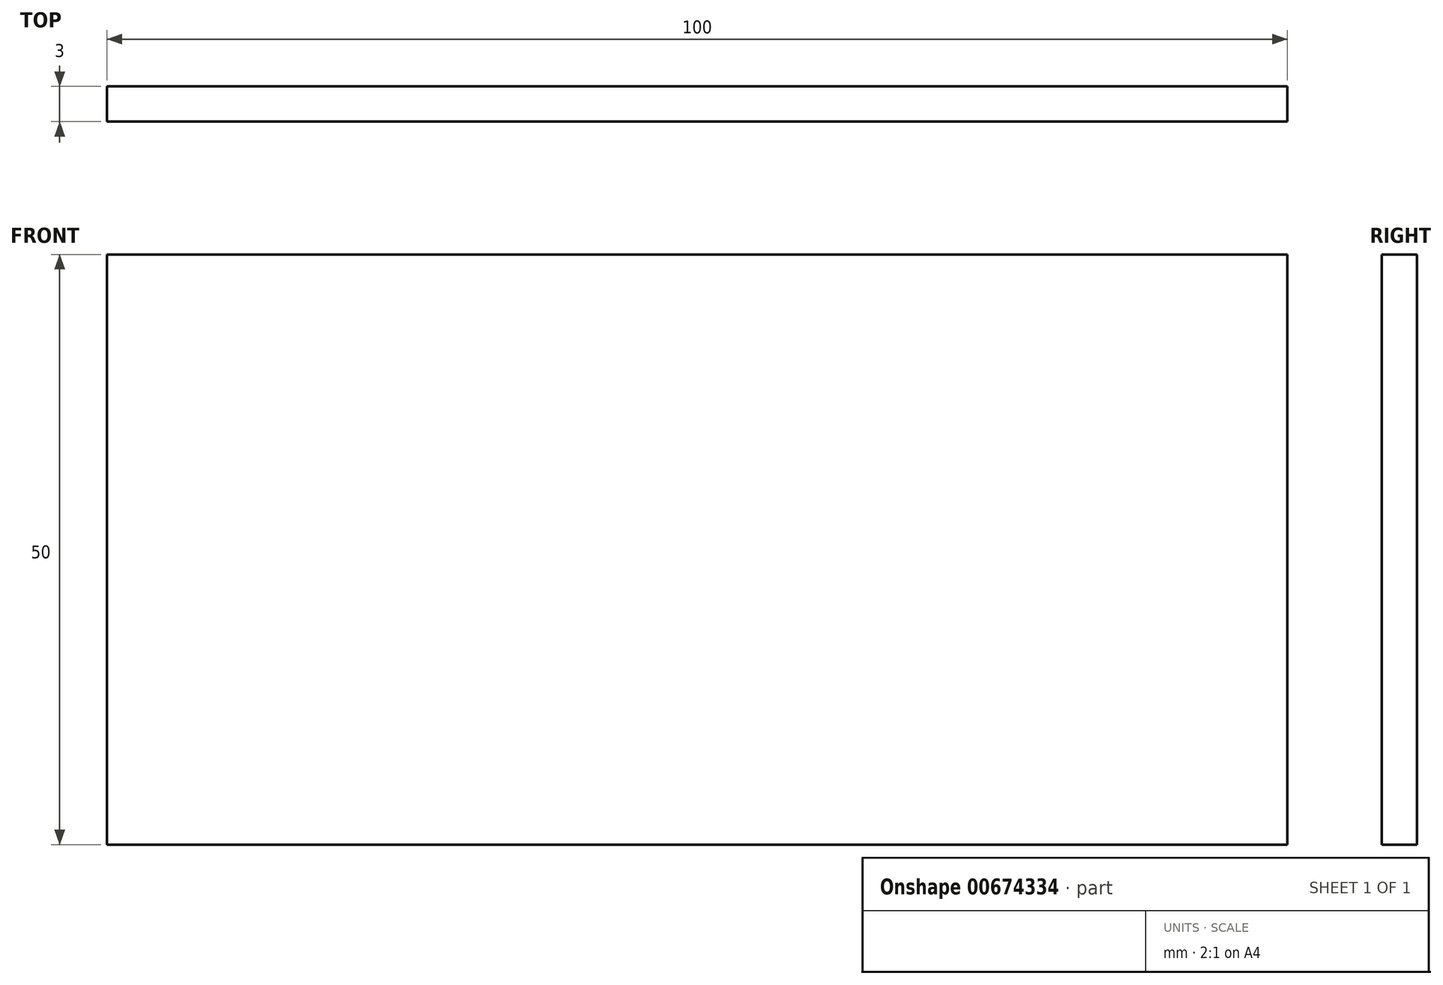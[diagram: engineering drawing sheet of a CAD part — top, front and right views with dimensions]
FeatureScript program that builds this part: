
annotation { "Feature Type Name" : "Feature", "Feature Type Description" : "" }
export const myFeature = defineFeature(function(context is Context, id is Id, definition is map)
    precondition{}
    {
        {
            var Q0;
            Q0=qCreatedBy(makeId("Front.planeOp"),FACE);
            var sketch = newSketch(context, id + "F0", { "sketchPlane" : qUnion([Q0])});
            skLineSegment(sketch, "E0.bottom", {"start": v(50, 25) * mm, "end": v(-50, 25) * mm});
            skLineSegment(sketch, "E0.top", {"start": v(50, -25) * mm, "end": v(-50, -25) * mm});
            skLineSegment(sketch, "E0.left", {"start": v(50, 25) * mm, "end": v(50, -25) * mm});
            skLineSegment(sketch, "E0.right", {"start": v(-50, 25) * mm, "end": v(-50, -25) * mm});
            skPoint(sketch, "E0.middle", {"position": v(0, 0) * mm});
            skSolve(sketch);
        }
        {
            var Q0;
            Q0=makeQuery(id+"F0.imprint","IMPRINT",FACE,{"disambiguationData":[TD([[makeQuery(id+"F0.imprint","IMPRINT",EDGE,{"derivedFrom":sQuery(id+"F0.wireOp",EDGE,"E0.bottom")}),1.0]])]});
            extrude(context, id + "F1", {"entities" : qUnion([Q0]), "depth" : 3 * mm, "offsetDistance" : 25 * mm});
        }
    });
